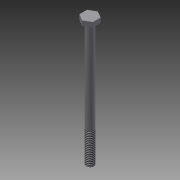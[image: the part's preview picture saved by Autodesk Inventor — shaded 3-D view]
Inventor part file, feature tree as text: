
AUTODESK INVENTOR PART (.ipt)
format: ipt  version: 2015 SP1 (Build 190203100, 203)  size: 88,064 bytes
history: native  units: in
note: dims shown in document units (in); Inventor stores cm internally (conversion verified against a paired STEP export)
features: extrude x2, sketch x2, thread x1
ambient origin geometry x8: Origin, YZ Plane, XZ Plane, XY Plane, X Axis, Y Axis, Z Axis, Center Point
bodies: Solid1 (feature_tree)
feature tree (5):
  extrude  "Extrusion1"  Depth=4.0in TaperAngle=0.0deg
  extrude  "Extrusion2"  Depth=0.4375in
  thread  "Thread1"  [1 undecoded]
  sketch  "Sketch1"  dims[d0=0.25in d1=4.0in d2=0.0in]
  sketch  "Sketch2"  dims[d3=0.4375in d4=0.4375in d5=0.4375in d6=120.0deg d7=120.0deg d8=0.2188in d9=0.2188in d10=0.2188in d11=0.1562in d12=0.0in d13=1.0in d14=3.0in]
note: 1 required parameter value undecoded (feature->parameter linkage not recoverable at this tier; creation-order binding heuristic only, values carry confidence <= 0.55)
